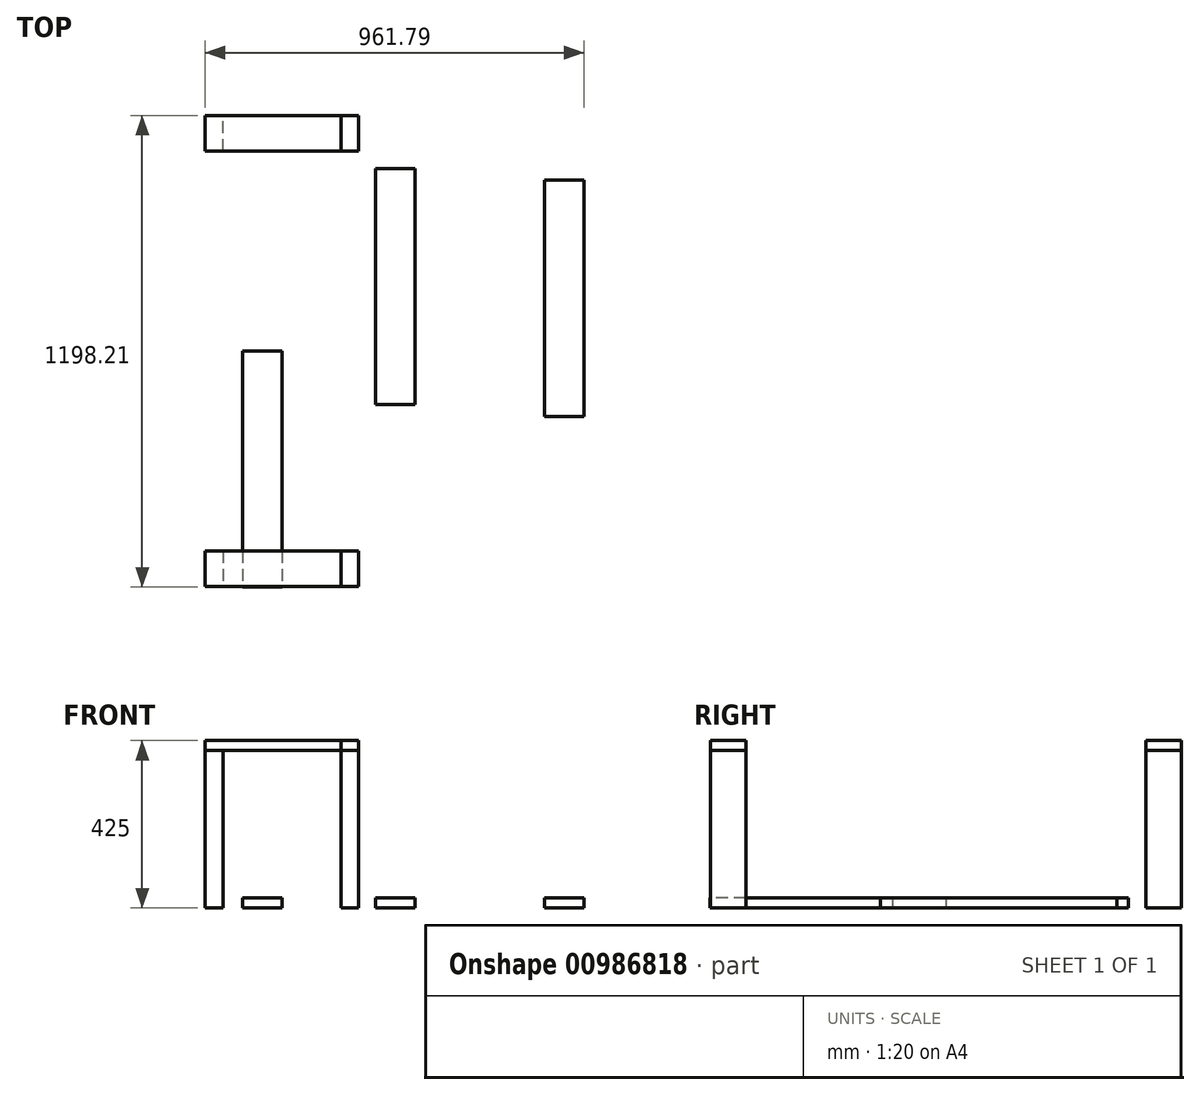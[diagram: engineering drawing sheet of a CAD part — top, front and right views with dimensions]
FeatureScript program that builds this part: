
annotation { "Feature Type Name" : "Feature", "Feature Type Description" : "" }
export const myFeature = defineFeature(function(context is Context, id is Id, definition is map)
    precondition{}
    {
        {
            var Q0;
            Q0=qCreatedBy(makeId("Top.planeOp"),FACE);
            var sketch = newSketch(context, id + "F0", { "sketchPlane" : qUnion([Q0])});
            skLineSegment(sketch, "E0", {"start": v(0, 37.56) * mm, "end": v(22.5, 37.56) * mm});
            skLineSegment(sketch, "E1", {"start": v(0, 37.56) * mm, "end": v(-22.5, 37.56) * mm});
            skLineSegment(sketch, "E2", {"start": v(-22.5, 37.56) * mm, "end": v(-22.5, -7.44) * mm});
            skLineSegment(sketch, "E3", {"start": v(-22.5, -7.44) * mm, "end": v(22.5, -7.44) * mm});
            skLineSegment(sketch, "E4", {"start": v(22.5, -7.44) * mm, "end": v(22.5, 37.56) * mm});
            skLineSegment(sketch, "E5.bottom", {"start": v(-150, -508.21) * mm, "end": v(-195, -508.21) * mm});
            skLineSegment(sketch, "E5.top", {"start": v(-150, -598.21) * mm, "end": v(-195, -598.21) * mm});
            skLineSegment(sketch, "E5.left", {"start": v(-150, -508.21) * mm, "end": v(-150, -598.21) * mm});
            skLineSegment(sketch, "E5.right", {"start": v(-195, -508.21) * mm, "end": v(-195, -598.21) * mm});
            skLineSegment(sketch, "E6.bottom", {"start": v(150, -508.21) * mm, "end": v(195, -508.21) * mm});
            skLineSegment(sketch, "E6.top", {"start": v(150, -598.21) * mm, "end": v(195, -598.21) * mm});
            skLineSegment(sketch, "E6.left", {"start": v(150, -508.21) * mm, "end": v(150, -598.21) * mm});
            skLineSegment(sketch, "E6.right", {"start": v(195, -508.21) * mm, "end": v(195, -598.21) * mm});
            skSolve(sketch);
        }
        {
            var Q0;
            Q0=makeQuery(id+"F0.imprint","IMPRINT",FACE,{"disambiguationData":[TD([[makeQuery(id+"F0.imprint","IMPRINT",EDGE,{"derivedFrom":sQuery(id+"F0.wireOp",EDGE,"E5.bottom")}),1.0]])]});
            var Q1;
            Q1=makeQuery(id+"F0.imprint","IMPRINT",FACE,{"disambiguationData":[TD([[makeQuery(id+"F0.imprint","IMPRINT",EDGE,{"derivedFrom":sQuery(id+"F0.wireOp",EDGE,"E6.bottom")}),-1.0]])]});
            extrude(context, id + "F1", {"entities" : qUnion([Q0, Q1]), "depth" : 400 * mm, "offsetDistance" : 25 * mm});
        }
        {
            var Q0;
            Q0=makeQuery(id+"F1.opExtrude","CAP_FACE",FACE,{"disambiguationData":[OSD([sQuery(id+"F0.wireOp",EDGE,"E6.bottom"),sQuery(id+"F0.wireOp",EDGE,"E6.top"),sQuery(id+"F0.wireOp",EDGE,"E6.left"),sQuery(id+"F0.wireOp",EDGE,"E6.right")])],"isStart":false});
            var sketch = newSketch(context, id + "F2", { "sketchPlane" : qUnion([Q0])});
            skLineSegment(sketch, "E7.bottom", {"start": v(150, -508.21) * mm, "end": v(195, -508.21) * mm});
            skLineSegment(sketch, "E7.top", {"start": v(150, -598.21) * mm, "end": v(195, -598.21) * mm});
            skLineSegment(sketch, "E7.left", {"start": v(150, -508.21) * mm, "end": v(150, -598.21) * mm});
            skLineSegment(sketch, "E7.right", {"start": v(195, -508.21) * mm, "end": v(195, -598.21) * mm});
            skSolve(sketch);
        }
        {
            var Q0;
            Q0=makeQuery(id+"FIzx0kF20QHHO79_2.boolean.opBoolean","MERGE",FACE,{"derivedFrom":[makeQuery(id+"F1.opExtrude","SWEPT_FACE",FACE,{"disambiguationData":[OSD([sQuery(id+"F0.wireOp",EDGE,"E6.left")])]}),makeQuery(id+"FIzx0kF20QHHO79_2.opExtrude","SWEPT_FACE",FACE,{"disambiguationData":[OSD([sQuery(id+"F2.wireOp",EDGE,"E7.left")])]})]});
            var sketch = newSketch(context, id + "F3", { "sketchPlane" : qUnion([Q0])});
            skLineSegment(sketch, "E8.bottom", {"start": v(508.21, 425) * mm, "end": v(598.21, 425) * mm});
            skLineSegment(sketch, "E8.top", {"start": v(508.21, 400) * mm, "end": v(598.21, 400) * mm});
            skLineSegment(sketch, "E8.left", {"start": v(508.21, 425) * mm, "end": v(508.21, 400) * mm});
            skLineSegment(sketch, "E8.right", {"start": v(598.21, 425) * mm, "end": v(598.21, 400) * mm});
            skSolve(sketch);
        }
        {
            var Q0;
            Q0=makeQuery(id+"F3.imprint","IMPRINT",FACE,{"disambiguationData":[TD([[makeQuery(id+"F3.imprint","IMPRINT",EDGE,{"derivedFrom":sQuery(id+"F3.wireOp",EDGE,"E8.bottom")}),-1.0]])]});
            extrude(context, id + "F4", {"entities" : qUnion([Q0]), "depth" : 345 * mm, "offsetDistance" : 25 * mm});
        }
        {
            var Q0;
            Q0=makeQuery(id+"F4.opExtrude","CAP_FACE",FACE,{"disambiguationData":[OSD([sQuery(id+"F3.wireOp",EDGE,"E8.bottom"),sQuery(id+"F3.wireOp",EDGE,"E8.top"),sQuery(id+"F3.wireOp",EDGE,"E8.left"),sQuery(id+"F3.wireOp",EDGE,"E8.right")])],"isStart":true});
            var sketch = newSketch(context, id + "F5", { "sketchPlane" : qUnion([Q0])});
            skSolve(sketch);
        }
        {
            var Q0;
            Q0 = qSketchRegion(id + "F5", true);
            var Q1;
            Q1=makeQuery(id+"F5.imprint","IMPRINT",FACE,{"disambiguationData":[TD([[makeQuery(id+"F5.imprint","IMPRINT",EDGE,{"derivedFrom":makeQuery(id+"F4.opExtrude","CAP_EDGE",EDGE,{"disambiguationData":[OSD([sQuery(id+"F3.wireOp",EDGE,"E8.bottom")])],"isStart":true})}),1.0]])]});
            extrude(context, id + "F6", {"entities" : qUnion([Q0, Q1]), "depth" : 45 * mm, "offsetDistance" : 25 * mm});
        }
        {
            var Q0;
            Q0=makeQuery(id+"F1.opExtrude","SWEPT_BODY",BODY,{"disambiguationData":[OSD([sQuery(id+"F0.wireOp",EDGE,"E5.bottom"),sQuery(id+"F0.wireOp",EDGE,"E5.top"),sQuery(id+"F0.wireOp",EDGE,"E5.left"),sQuery(id+"F0.wireOp",EDGE,"E5.right")])]});
            var Q1;
            Q1=makeQuery(id+"F1.opExtrude","SWEPT_BODY",BODY,{"disambiguationData":[OSD([sQuery(id+"F0.wireOp",EDGE,"E6.bottom"),sQuery(id+"F0.wireOp",EDGE,"E6.top"),sQuery(id+"F0.wireOp",EDGE,"E6.left"),sQuery(id+"F0.wireOp",EDGE,"E6.right")])]});
            var Q2;
            Q2=makeQuery(id+"F4.opExtrude","SWEPT_BODY",BODY,{"disambiguationData":[OSD([sQuery(id+"F3.wireOp",EDGE,"E8.bottom"),sQuery(id+"F3.wireOp",EDGE,"E8.top"),sQuery(id+"F3.wireOp",EDGE,"E8.left"),sQuery(id+"F3.wireOp",EDGE,"E8.right")])]});
            var Q3;
            Q3=makeQuery(id+"F6.opExtrude","SWEPT_BODY",BODY,{"disambiguationData":[OSD([sQuery(id+"F3.wireOp",EDGE,"E8.bottom"),sQuery(id+"F3.wireOp",EDGE,"E8.top"),sQuery(id+"F3.wireOp",EDGE,"E8.left"),sQuery(id+"F3.wireOp",EDGE,"E8.right")])]});
            var Q4;
            Q4=qCreatedBy(makeId("Front.planeOp"),FACE);
            mirror(context, id + "F7", {"entities" : qUnion([Q0, Q1, Q2, Q3]), "mirrorPlane" : qUnion([Q4])});
        }
        {
            var Q0;
            Q0=qCreatedBy(makeId("Top.planeOp"),FACE);
            var sketch = newSketch(context, id + "F8", { "sketchPlane" : qUnion([Q0])});
            skLineSegment(sketch, "E9.bottom", {"start": v(0, 0) * mm, "end": v(-100, 0) * mm});
            skLineSegment(sketch, "E9.top", {"start": v(0, -600) * mm, "end": v(-100, -600) * mm});
            skLineSegment(sketch, "E9.left", {"start": v(0, 0) * mm, "end": v(0, -600) * mm});
            skLineSegment(sketch, "E9.right", {"start": v(-100, 0) * mm, "end": v(-100, -600) * mm});
            skLineSegment(sketch, "E10.bottom", {"start": v(238, 463.89) * mm, "end": v(338, 463.89) * mm});
            skLineSegment(sketch, "E10.top", {"start": v(238, -136.11) * mm, "end": v(338, -136.11) * mm});
            skLineSegment(sketch, "E10.left", {"start": v(238, 463.89) * mm, "end": v(238, -136.11) * mm});
            skLineSegment(sketch, "E10.right", {"start": v(338, 463.89) * mm, "end": v(338, -136.11) * mm});
            skLineSegment(sketch, "E11.bottom", {"start": v(666.8, 433.81) * mm, "end": v(766.8, 433.81) * mm});
            skLineSegment(sketch, "E11.top", {"start": v(666.8, -166.19) * mm, "end": v(766.8, -166.19) * mm});
            skLineSegment(sketch, "E11.left", {"start": v(666.8, 433.81) * mm, "end": v(666.8, -166.19) * mm});
            skLineSegment(sketch, "E11.right", {"start": v(766.8, 433.81) * mm, "end": v(766.8, -166.19) * mm});
            skSolve(sketch);
        }
        {
            var Q0;
            Q0=makeQuery(id+"F8.imprint","IMPRINT",FACE,{"disambiguationData":[TD([[makeQuery(id+"F8.imprint","IMPRINT",EDGE,{"derivedFrom":sQuery(id+"F8.wireOp",EDGE,"E11.bottom")}),-1.0]])]});
            var Q1;
            Q1=makeQuery(id+"F8.imprint","IMPRINT",FACE,{"disambiguationData":[TD([[makeQuery(id+"F8.imprint","IMPRINT",EDGE,{"derivedFrom":sQuery(id+"F8.wireOp",EDGE,"E10.bottom")}),-1.0]])]});
            var Q2;
            Q2=makeQuery(id+"F8.imprint","IMPRINT",FACE,{"disambiguationData":[TD([[makeQuery(id+"F8.imprint","IMPRINT",EDGE,{"derivedFrom":sQuery(id+"F8.wireOp",EDGE,"E9.bottom")}),1.0]])]});
            extrude(context, id + "F9", {"entities" : qUnion([Q0, Q1, Q2]), "depth" : 25 * mm, "offsetDistance" : 25 * mm});
        }
    });
